# Revit family: Practibox_S_4_modules_encastré_réf_134004_à_134174
name_source: partatom
category: Equipement électrique
revit_build: Autodesk Revit 2018 (Build: 20170223_1515(x64)
units: mm (PartAtom-declared; Revit-internal decimal feet)

## family parameters
Basée sur le plan de construction = Non
Configuration du panneau = Deux colonnes, circuits au sein
Cote de connecteur circulaire = Utiliser le diamètre
Couper avec des vides une fois chargée = Non
Numéro OmniClass = 23.80.30.11.17
Partagée = Non
Point de calcul de pièce = Non
Titre OmniClass = Distribution Boards and Control Panels
Toujours verticalement = Oui
Type d'élément = Tableau de raccordement

## types (8) — shared parameters
Conditions Générale d'Utilisation = https://export.legrand.com
Fabricant = "Legrand"
Hauteur = 215 mm
Ina = 40 A
Largeur = 184 mm  [stored 0.603675 ft]
URL = www.legrand.com
profondeur = 100 mm  [stored 0.328084 ft]
taille = 4 modules

## per-type parameters (varying)
| type | Bornier N | Bornier T | porte blanche | porte transparente |
| Practibox_S_4_modules_encastré_134004 |  |  | Oui | Non |
| Practibox_S_4_modules_encastré_134014 |  |  | Non | Oui |
| Practibox_S_4_modules_encastré_134154 | 4 départs Icc 6kA | 4 départs Icc 6kA | Non | Oui |
| Practibox_S_4_modules_encastré_134144 | 4 départs Icc 6kA | 4 départs Icc 6kA | Oui | Non |
| Practibox_S_4_modules_encastré_134034 |  |  | Non | Oui |
| Practibox_S_4_modules_encastré_134174 | 4 départs Icc 6kA | 4 départs Icc 6kA | Non | Oui |
| Practibox_S_4_modules_encastré_134164 | 4 départs Icc 6kA | 4 départs Icc 6kA | Oui | Non |
| Practibox_S_4_modules_encastré_134024 |  |  | Oui | Non |

note: column(s) folded — value = type name in every type: Description

note: [stored X ft] marks values corroborated as IEEE doubles in the binary element streams (Revit-internal decimal feet)
